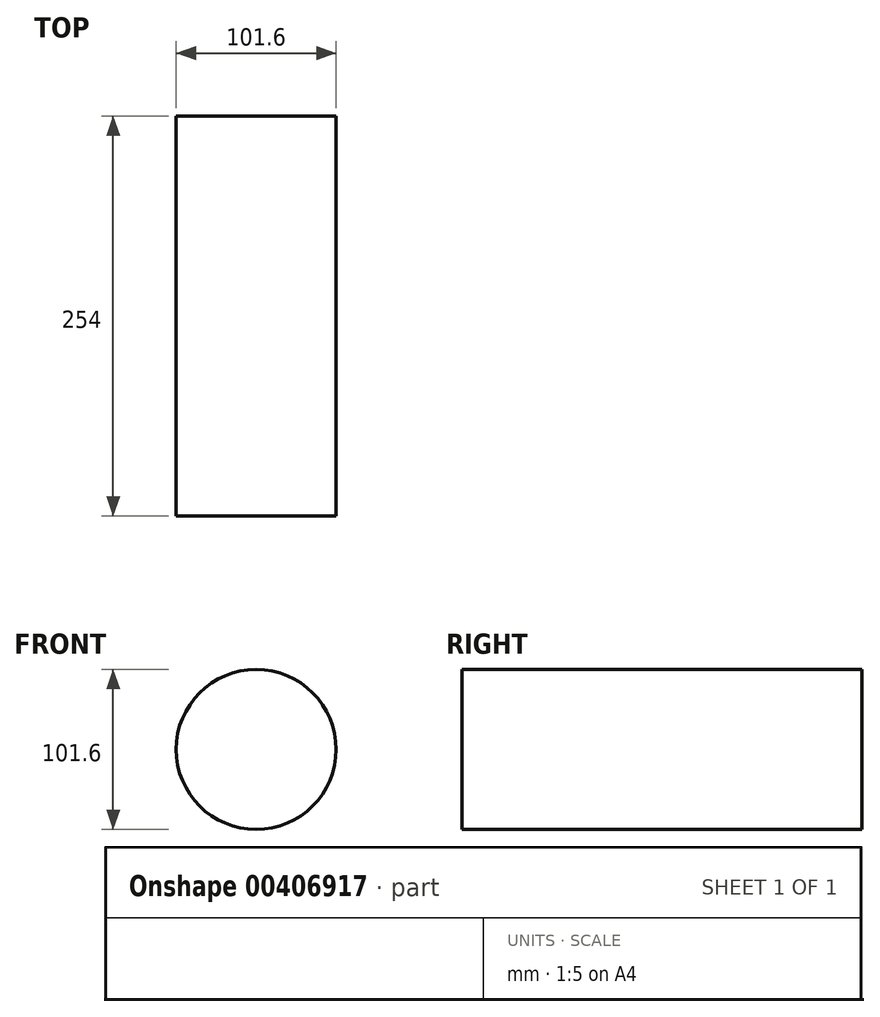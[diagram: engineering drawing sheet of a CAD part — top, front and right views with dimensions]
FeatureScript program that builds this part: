
annotation { "Feature Type Name" : "Feature", "Feature Type Description" : "" }
export const myFeature = defineFeature(function(context is Context, id is Id, definition is map)
    precondition{}
    {
        {
            var Q0;
            Q0=qCreatedBy(makeId("Front.planeOp"),FACE);
            var sketch = newSketch(context, id + "F0", { "sketchPlane" : qUnion([Q0])});
            skCircle(sketch, "E0", {"center": v(0, 0) * mm, "radius": 50.8 * mm});
            skSolve(sketch);
        }
        {
            var Q0;
            Q0=makeQuery(id+"F0.imprint","IMPRINT",FACE,{"disambiguationData":[TD([[makeQuery(id+"F0.imprint","IMPRINT",EDGE,{"derivedFrom":sQuery(id+"F0.wireOp",EDGE,"E0")}),1.0]])]});
            extrude(context, id + "F1", {"entities" : qUnion([Q0]), "depth" : 254 * mm});
        }
    });
